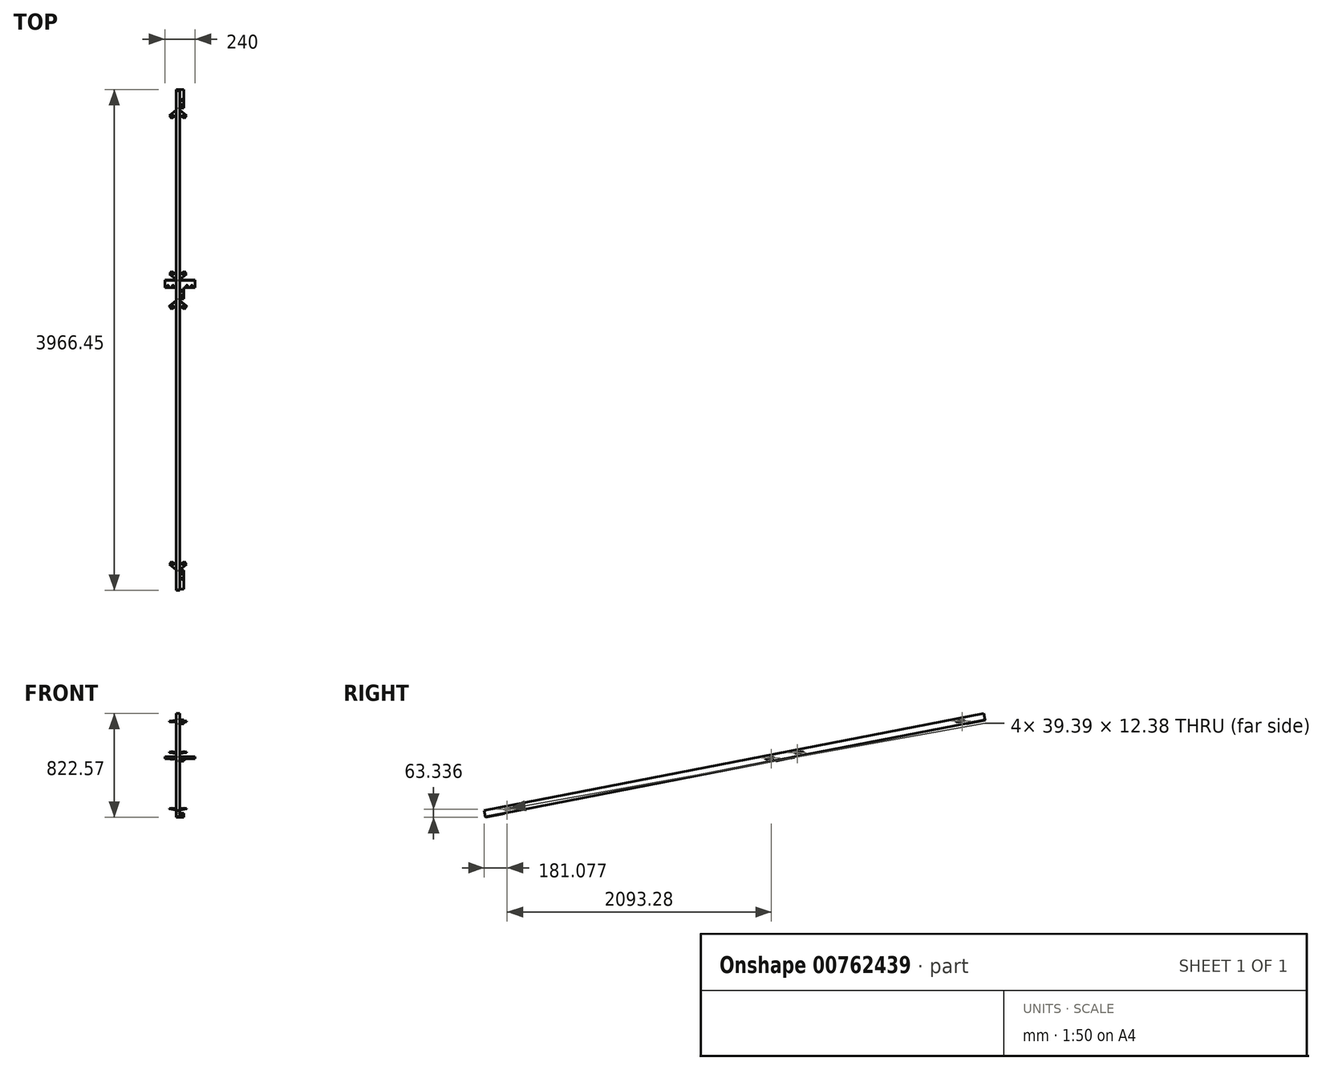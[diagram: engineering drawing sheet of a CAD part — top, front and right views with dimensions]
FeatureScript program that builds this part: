
annotation { "Feature Type Name" : "Feature", "Feature Type Description" : "" }
export const myFeature = defineFeature(function(context is Context, id is Id, definition is map)
    precondition{}
    {
        {
            var Q0;
            Q0=qCreatedBy(makeId("Top.planeOp"),FACE);
            var sketch = newSketch(context, id + "F0", { "sketchPlane" : qUnion([Q0])});
            skPoint(sketch, "E0", {"position": v(0, 0) * mm});
            skPoint(sketch, "E1", {"position": v(28.11, 0) * mm});
            skLineSegment(sketch, "E2", {"start": v(0, 0) * mm, "end": v(28.11, 0) * mm});
            skSolve(sketch);
        }
        {
            var Q0;
            Q0=qCreatedBy(makeId("Top.planeOp"),FACE);
            var Q1;
            Q1=sQuery(id+"F0.wireOp",EDGE,"E2");
            cPlane(context, id + "F1", {"entities" : qUnion([Q0, Q1]), "cplaneType" : CPlaneType.LINE_ANGLE, "offset" : 25 * mm, "angle" : 11 * degree, "width" : 150 * mm, "height" : 150 * mm});
        }
        {
            var Q0;
            Q0=qCreatedBy(id+"F1.planeOp",FACE);
            var Q1;
            Q1=sQuery(id+"F0.wireOp",EDGE,"E2");
            cPlane(context, id + "F2", {"entities" : qUnion([Q0, Q1]), "cplaneType" : CPlaneType.LINE_ANGLE, "offset" : 25 * mm, "angle" : 90 * degree, "width" : 150 * mm, "height" : 150 * mm});
        }
        {
            var Q0;
            Q0=qCreatedBy(id+"F2.planeOp",FACE);
            var sketch = newSketch(context, id + "F3", { "sketchPlane" : qUnion([Q0])});
            skLineSegment(sketch, "E3.bottom", {"start": v(15, -25) * mm, "end": v(-15, -25) * mm});
            skLineSegment(sketch, "E3.top", {"start": v(15, 25) * mm, "end": v(-15, 25) * mm});
            skLineSegment(sketch, "E3.left", {"start": v(15, -25) * mm, "end": v(15, 25) * mm});
            skLineSegment(sketch, "E3.right", {"start": v(-15, -25) * mm, "end": v(-15, 25) * mm});
            skPoint(sketch, "E3.middle", {"position": v(0, 0) * mm});
            skLineSegment(sketch, "E4.bottom", {"start": v(14, -24) * mm, "end": v(-14, -24) * mm});
            skLineSegment(sketch, "E4.top", {"start": v(14, 24) * mm, "end": v(-14, 24) * mm});
            skLineSegment(sketch, "E4.left", {"start": v(14, -24) * mm, "end": v(14, 24) * mm});
            skLineSegment(sketch, "E4.right", {"start": v(-14, -24) * mm, "end": v(-14, 24) * mm});
            skSolve(sketch);
        }
        {
            var Q0;
            Q0=qSketchRegion(id+"F3",true);
            extrude(context, id + "F4", {"entities" : qUnion([Q0]), "depth" : 30 * mm, "offsetDistance" : 25 * mm, "hasSecondDirection" : true, "secondDirectionOppositeDirection" : true, "secondDirectionDepth" : 4000 * mm});
        }
        {
            var Q0;
            Q0=makeQuery(id+"F4.opExtrude","SWEPT_FACE",FACE,{"disambiguationData":[OSD([sQuery(id+"F3.wireOp",EDGE,"E3.bottom")])]});
            var sketch = newSketch(context, id + "F5", { "sketchPlane" : qUnion([Q0])});
            skLineSegment(sketch, "E5.0", {"start": v(45, -4000) * mm, "end": v(135, -4000) * mm});
            skLineSegment(sketch, "E6.0", {"start": v(-15, -4000) * mm, "end": v(45, -4000) * mm});
            skLineSegment(sketch, "E7.0", {"start": v(-15, -4000) * mm, "end": v(-15, -3850) * mm});
            skLineSegment(sketch, "E8.0", {"start": v(-15, -3850) * mm, "end": v(45, -3850) * mm});
            skLineSegment(sketch, "E9.0", {"start": v(45, -3940) * mm, "end": v(45, -3850) * mm});
            skLineSegment(sketch, "E10.0", {"start": v(45, -3940) * mm, "end": v(135, -3940) * mm});
            skLineSegment(sketch, "E11.0", {"start": v(135, -4000) * mm, "end": v(135, -3940) * mm});
            skCircle(sketch, "E12.0", {"center": v(70, -3955) * mm, "radius": 6 * mm});
            skCircle(sketch, "E13.0", {"center": v(110, -3955) * mm, "radius": 6 * mm});
            skCircle(sketch, "E14.0", {"center": v(30, -3915) * mm, "radius": 6 * mm});
            skCircle(sketch, "E15.0", {"center": v(30, -3875) * mm, "radius": 6 * mm});
            skLineSegment(sketch, "E16", {"start": v(45, -3940) * mm, "end": v(45, -4000) * mm});
            skSolve(sketch);
        }
        {
            var Q0;
            {var subQ0=sQuery(id+"F5.wireOp",EDGE,"E9.0");Q0=makeQuery(id+"F5.imprint","IMPRINT",FACE,{"disambiguationData":[TD([[makeQuery(id+"F5.imprint","IMPRINT",EDGE,{"derivedFrom":subQ0}),1.0]])]});}
            var Q1;
            {var subQ4=sQuery(id+"F5.wireOp",EDGE,"E7.0");Q1=makeQuery(id+"F5.imprint","IMPRINT",FACE,{"disambiguationData":[TD([[makeQuery(id+"F5.imprint","IMPRINT",EDGE,{"derivedFrom":subQ4}),1.0]])]});}
            extrude(context, id + "F6", {"entities" : qUnion([Q0, Q1]), "operationType" : NewBodyOperationType.ADD, "depth" : 5 * mm, "offsetDistance" : 25 * mm});
        }
        {
            var Q0;
            Q0=makeQuery(id+"F4.opExtrude","SWEPT_FACE",FACE,{"disambiguationData":[OSD([sQuery(id+"F3.wireOp",EDGE,"E3.bottom")])]});
            var sketch = newSketch(context, id + "F7", { "sketchPlane" : qUnion([Q0])});
            skLineSegment(sketch, "E17.0", {"start": v(45, -2401.65) * mm, "end": v(45, -2311.65) * mm});
            skLineSegment(sketch, "E18.0", {"start": v(-15, -2311.65) * mm, "end": v(45, -2311.65) * mm});
            skLineSegment(sketch, "E19.0", {"start": v(-15, -2461.65) * mm, "end": v(135, -2461.65) * mm});
            skLineSegment(sketch, "E20.0", {"start": v(135, -2461.65) * mm, "end": v(135, -2401.65) * mm});
            skLineSegment(sketch, "E21.0", {"start": v(45, -2401.65) * mm, "end": v(135, -2401.65) * mm});
            skLineSegment(sketch, "E22", {"start": v(-15, -2461.65) * mm, "end": v(-15, -2311.65) * mm});
            skLineSegment(sketch, "E23", {"start": v(45, -2401.65) * mm, "end": v(45, -2461.65) * mm});
            skCircle(sketch, "E24.0", {"center": v(30, -2376.65) * mm, "radius": 6 * mm});
            skCircle(sketch, "E25.0", {"center": v(30, -2336.65) * mm, "radius": 6 * mm});
            skLineSegment(sketch, "E26", {"start": v(15, -2311.65) * mm, "end": v(15, -2461.65) * mm, "construction": true});
            skLineSegment(sketch, "E27.MirrorCS", {"start": v(45, -2461.65) * mm, "end": v(-105, -2461.65) * mm});
            skLineSegment(sketch, "E28.MirrorCS", {"start": v(-15, -2401.65) * mm, "end": v(-105, -2401.65) * mm});
            skLineSegment(sketch, "E29.MirrorCS", {"start": v(-105, -2461.65) * mm, "end": v(-105, -2401.65) * mm});
            skLineSegment(sketch, "E30", {"start": v(45, -2401.65) * mm, "end": v(76.32, -2370.32) * mm});
            skCircle(sketch, "E31.MirrorC", {"center": v(70, -2416.65) * mm, "radius": 6 * mm});
            skCircle(sketch, "E32.MirrorC", {"center": v(110, -2416.65) * mm, "radius": 6 * mm});
            skCircle(sketch, "E33.MirrorC", {"center": v(-40, -2416.65) * mm, "radius": 6 * mm});
            skCircle(sketch, "E34.MirrorC", {"center": v(-80, -2416.65) * mm, "radius": 6 * mm});
            skSolve(sketch);
        }
        {
            var Q0;
            {var subQ0=sQuery(id+"F7.wireOp",EDGE,"E22");Q0=makeQuery(id+"F7.imprint","IMPRINT",FACE,{"disambiguationData":[TD([[makeQuery(id+"F7.imprint","IMPRINT",EDGE,{"derivedFrom":subQ0}),1.0]])]});}
            var Q1;
            {var subQ7=sQuery(id+"F7.wireOp",EDGE,"E17.0");Q1=makeQuery(id+"F7.imprint","IMPRINT",FACE,{"disambiguationData":[TD([[makeQuery(id+"F7.imprint","IMPRINT",EDGE,{"derivedFrom":subQ7}),1.0]])]});}
            var Q2;
            {var subQ3=sQuery(id+"F7.wireOp",EDGE,"E28.MirrorCS");Q2=makeQuery(id+"F7.imprint","IMPRINT",FACE,{"disambiguationData":[TD([[makeQuery(id+"F7.imprint","IMPRINT",EDGE,{"derivedFrom":subQ3}),1.0]])]});}
            var Q3;
            {var subQ2=sQuery(id+"F7.wireOp",EDGE,"E20.0");Q3=makeQuery(id+"F7.imprint","IMPRINT",FACE,{"disambiguationData":[TD([[makeQuery(id+"F7.imprint","IMPRINT",EDGE,{"derivedFrom":subQ2}),1.0]])]});}
            extrude(context, id + "F8", {"entities" : qUnion([Q0, Q1, Q2, Q3]), "operationType" : NewBodyOperationType.ADD, "depth" : 5 * mm, "offsetDistance" : 25 * mm});
        }
        {
            var Q0;
            {var subQ3=sQuery(id+"F3.wireOp",EDGE,"E3.bottom");var subQ4=sQuery(id+"F7.wireOp",EDGE,"E18.0");Q0=makeQuery(id+"F8.boolean.opBoolean","SPLIT",FACE,{"disambiguationData":[TD([makeQuery(id+"F8.opExtrude","SWEPT_FACE",FACE,{"disambiguationData":[OSD([subQ4])]})])],"derivedFrom":makeQuery(id+"F4.opExtrude","SWEPT_FACE",FACE,{"disambiguationData":[OSD([subQ3])]})});}
            var sketch = newSketch(context, id + "F9", { "sketchPlane" : qUnion([Q0])});
            skLineSegment(sketch, "E35.0", {"start": v(-15, -120.03) * mm, "end": v(45, -120.03) * mm});
            skLineSegment(sketch, "E36.0", {"start": v(45, -30.03) * mm, "end": v(45, -120.03) * mm});
            skCircle(sketch, "E37.0", {"center": v(30, -95.03) * mm, "radius": 6 * mm});
            skCircle(sketch, "E38.0", {"center": v(30, -55.03) * mm, "radius": 6 * mm});
            skLineSegment(sketch, "E39.0", {"start": v(45, -30.03) * mm, "end": v(135, -30.03) * mm});
            skLineSegment(sketch, "E40.0", {"start": v(-15, 29) * mm, "end": v(135, 29) * mm});
            skLineSegment(sketch, "E41", {"start": v(-15, -120.03) * mm, "end": v(-15, 29) * mm});
            skLineSegment(sketch, "E42", {"start": v(45, -30.03) * mm, "end": v(45, 30) * mm});
            skSolve(sketch);
        }
        {
            var Q0;
            Q0=qSketchRegion(id+"F9",true);
            extrude(context, id + "F10", {"entities" : qUnion([Q0]), "operationType" : NewBodyOperationType.ADD, "depth" : 4.8 * mm, "offsetDistance" : 25 * mm});
        }
        {
            var Q0;
            Q0=qCreatedBy(id+"F1.planeOp",FACE);
            var sketch = newSketch(context, id + "F11", { "sketchPlane" : qUnion([Q0])});
            skLineSegment(sketch, "E43.0", {"start": v(15, -3850) * mm, "end": v(45, -3850) * mm});
            skLineSegment(sketch, "E44", {"start": v(15, -3850) * mm, "end": v(15, -3840) * mm});
            skLineSegment(sketch, "E45", {"start": v(41, -1985.01) * mm, "end": v(15.07, -1985.01) * mm});
            skLineSegment(sketch, "E46.MirrorCS", {"start": v(15, -3840) * mm, "end": v(68.63, -3795) * mm});
            skLineSegment(sketch, "E47.MirrorCS", {"start": v(68.63, -3795) * mm, "end": v(49.34, -3772.03) * mm});
            skLineSegment(sketch, "E48.MirrorCS", {"start": v(49.34, -3772.03) * mm, "end": v(14.87, -3800.95) * mm});
            skCircle(sketch, "E49.MirrorC", {"center": v(43.27, -3796.7) * mm, "radius": 6 * mm});
            skLineSegment(sketch, "E50.MirrorCS", {"start": v(43.27, -3796.7) * mm, "end": v(58.99, -3783.52) * mm, "construction": true});
            skLineSegment(sketch, "E51", {"start": v(15, -3840) * mm, "end": v(14.87, -3800.95) * mm});
            skLineSegment(sketch, "E52.MirrorCS", {"start": v(15, -130.03) * mm, "end": v(68.63, -175.02) * mm});
            skCircle(sketch, "E53.MirrorC", {"center": v(43.27, -173.32) * mm, "radius": 6 * mm});
            skLineSegment(sketch, "E54.MirrorCS", {"start": v(43.27, -173.32) * mm, "end": v(58.99, -186.5) * mm, "construction": true});
            skLineSegment(sketch, "E55.MirrorCS", {"start": v(68.63, -175.02) * mm, "end": v(49.34, -198) * mm});
            skLineSegment(sketch, "E56.MirrorCS", {"start": v(49.34, -198) * mm, "end": v(14.87, -169.08) * mm});
            skLineSegment(sketch, "E57.MirrorCS", {"start": v(15, -130.03) * mm, "end": v(14.87, -169.08) * mm});
            skPoint(sketch, "E58.0", {"position": v(30, -2311.65) * mm});
            skLineSegment(sketch, "E59.0", {"start": v(15, -2311.65) * mm, "end": v(45, -2311.65) * mm});
            skLineSegment(sketch, "E60.0", {"start": v(15, -2461.65) * mm, "end": v(135, -2461.65) * mm});
            skLineSegment(sketch, "E61", {"start": v(15, -2311.65) * mm, "end": v(15, -2301.65) * mm});
            skLineSegment(sketch, "E62", {"start": v(15, -2461.65) * mm, "end": v(15, -2471.65) * mm});
            skLineSegment(sketch, "E63", {"start": v(15, -2301.65) * mm, "end": v(15, -130.03) * mm});
            skLineSegment(sketch, "E64", {"start": v(45.74, -1215.84) * mm, "end": v(15, -1215.84) * mm});
            skLineSegment(sketch, "E65.MirrorCS", {"start": v(49.34, -2233.67) * mm, "end": v(14.87, -2262.6) * mm});
            skLineSegment(sketch, "E66.MirrorCS", {"start": v(15, -2301.65) * mm, "end": v(14.87, -2262.6) * mm});
            skLineSegment(sketch, "E67.MirrorCS", {"start": v(15, -2301.65) * mm, "end": v(68.63, -2256.65) * mm});
            skLineSegment(sketch, "E68.MirrorCS", {"start": v(68.63, -2256.65) * mm, "end": v(49.34, -2233.67) * mm});
            skLineSegment(sketch, "E69.MirrorCS", {"start": v(43.27, -2258.35) * mm, "end": v(58.99, -2245.16) * mm, "construction": true});
            skCircle(sketch, "E70.MirrorC", {"center": v(43.27, -2258.35) * mm, "radius": 6 * mm});
            skLineSegment(sketch, "E71", {"start": v(15, -2471.65) * mm, "end": v(15, -3840) * mm});
            skLineSegment(sketch, "E72", {"start": v(29.54, -3155.82) * mm, "end": v(15, -3155.82) * mm});
            skLineSegment(sketch, "E73.MirrorCS", {"start": v(15, -2471.65) * mm, "end": v(68.63, -2516.64) * mm});
            skLineSegment(sketch, "E74.MirrorCS", {"start": v(15, -2471.65) * mm, "end": v(14.87, -2510.7) * mm});
            skLineSegment(sketch, "E75.MirrorCS", {"start": v(49.34, -2539.62) * mm, "end": v(14.87, -2510.7) * mm});
            skLineSegment(sketch, "E76.MirrorCS", {"start": v(68.63, -2516.64) * mm, "end": v(49.34, -2539.62) * mm});
            skCircle(sketch, "E77.MirrorC", {"center": v(43.27, -2514.94) * mm, "radius": 6 * mm});
            skLineSegment(sketch, "E78.MirrorCS", {"start": v(43.27, -2514.94) * mm, "end": v(58.99, -2528.13) * mm, "construction": true});
            skLineSegment(sketch, "E79", {"start": v(15, -3840) * mm, "end": v(-15, -3840.1) * mm, "construction": true});
            skLineSegment(sketch, "E80", {"start": v(0, -3840.05) * mm, "end": v(0, -129.98) * mm, "construction": true});
            skLineSegment(sketch, "E81", {"start": v(15, -130.03) * mm, "end": v(0, -129.98) * mm, "construction": true});
            skLineSegment(sketch, "E82.MirrorCS", {"start": v(-49.34, -198) * mm, "end": v(-14.87, -169.08) * mm});
            skLineSegment(sketch, "E83.MirrorCS", {"start": v(-68.63, -175.02) * mm, "end": v(-49.34, -198) * mm});
            skLineSegment(sketch, "E84.MirrorCS", {"start": v(-15, -130.03) * mm, "end": v(-68.63, -175.02) * mm});
            skCircle(sketch, "E85.MirrorC", {"center": v(-43.27, -173.32) * mm, "radius": 6 * mm});
            skLineSegment(sketch, "E86.MirrorCS", {"start": v(-43.27, -173.32) * mm, "end": v(-58.99, -186.5) * mm, "construction": true});
            skLineSegment(sketch, "E87.MirrorCS", {"start": v(-15, -2301.65) * mm, "end": v(-68.63, -2256.65) * mm});
            skCircle(sketch, "E88.MirrorC", {"center": v(-43.27, -2258.35) * mm, "radius": 6 * mm});
            skLineSegment(sketch, "E89.MirrorCS", {"start": v(-49.34, -2233.67) * mm, "end": v(-14.87, -2262.6) * mm});
            skLineSegment(sketch, "E90.MirrorCS", {"start": v(-15, -2301.65) * mm, "end": v(-15, -130.03) * mm});
            skLineSegment(sketch, "E91.MirrorCS", {"start": v(-68.63, -2256.65) * mm, "end": v(-49.34, -2233.67) * mm});
            skLineSegment(sketch, "E92.MirrorCS", {"start": v(-15, -2471.65) * mm, "end": v(-68.63, -2516.64) * mm});
            skLineSegment(sketch, "E93.MirrorCS", {"start": v(-49.34, -2539.62) * mm, "end": v(-14.87, -2510.7) * mm});
            skLineSegment(sketch, "E94.MirrorCS", {"start": v(-68.63, -2516.64) * mm, "end": v(-49.34, -2539.62) * mm});
            skCircle(sketch, "E95.MirrorC", {"center": v(-43.27, -2514.94) * mm, "radius": 6 * mm});
            skLineSegment(sketch, "E96.MirrorCS", {"start": v(-43.27, -2514.94) * mm, "end": v(-58.99, -2528.13) * mm, "construction": true});
            skLineSegment(sketch, "E97.MirrorCS", {"start": v(-15, -3840) * mm, "end": v(-68.63, -3795) * mm});
            skCircle(sketch, "E98.MirrorC", {"center": v(-43.27, -3796.7) * mm, "radius": 6 * mm});
            skLineSegment(sketch, "E99.MirrorCS", {"start": v(-49.34, -3772.03) * mm, "end": v(-14.87, -3800.95) * mm});
            skLineSegment(sketch, "E100.MirrorCS", {"start": v(-68.63, -3795) * mm, "end": v(-49.34, -3772.03) * mm});
            skLineSegment(sketch, "E101.MirrorCS", {"start": v(-43.27, -3796.7) * mm, "end": v(-58.99, -3783.52) * mm, "construction": true});
            skLineSegment(sketch, "E102", {"start": v(-15, -3840) * mm, "end": v(-14.87, -3800.95) * mm});
            skLineSegment(sketch, "E103", {"start": v(-14.87, -2510.7) * mm, "end": v(-15, -2471.65) * mm});
            skSolve(sketch);
        }
        {
            var Q0;
            Q0=qSketchRegion(id+"F11",true);
            extrude(context, id + "F12", {"entities" : qUnion([Q0]), "operationType" : NewBodyOperationType.ADD, "depth" : 2.5 * mm, "offsetDistance" : 25 * mm, "hasSecondDirection" : true, "secondDirectionOppositeDirection" : true, "secondDirectionDepth" : 2.5 * mm});
        }
    });
